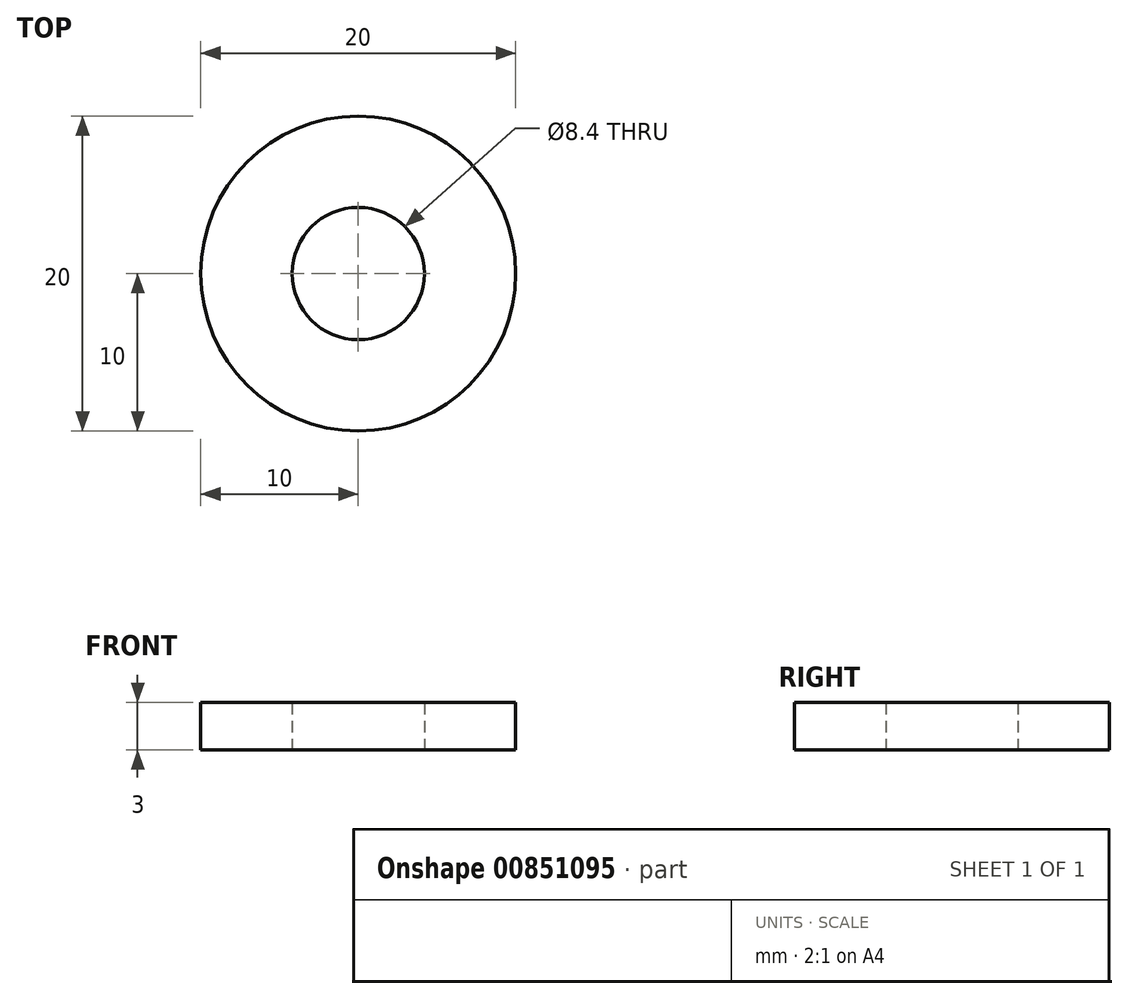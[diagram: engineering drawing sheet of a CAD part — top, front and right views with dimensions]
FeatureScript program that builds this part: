
annotation { "Feature Type Name" : "Feature", "Feature Type Description" : "" }
export const myFeature = defineFeature(function(context is Context, id is Id, definition is map)
    precondition{}
    {
        {
            var Q0;
            Q0=qCreatedBy(makeId("Top.planeOp"),FACE);
            var sketch = newSketch(context, id + "F0", { "sketchPlane" : qUnion([Q0])});
            skCircle(sketch, "E0", {"center": v(0, 0) * mm, "radius": 10 * mm});
            skCircle(sketch, "E1", {"center": v(0, 0) * mm, "radius": 4.2 * mm});
            skSolve(sketch);
        }
        {
            var Q0;
            Q0=makeQuery(id+"F0.imprint","IMPRINT",FACE,{"disambiguationData":[TD([[makeQuery(id+"F0.imprint","IMPRINT",EDGE,{"derivedFrom":sQuery(id+"F0.wireOp",EDGE,"E0")}),1.0]])]});
            extrude(context, id + "F1", {"entities" : qUnion([Q0]), "depth" : 3 * mm, "offsetDistance" : 25 * mm});
        }
    });
